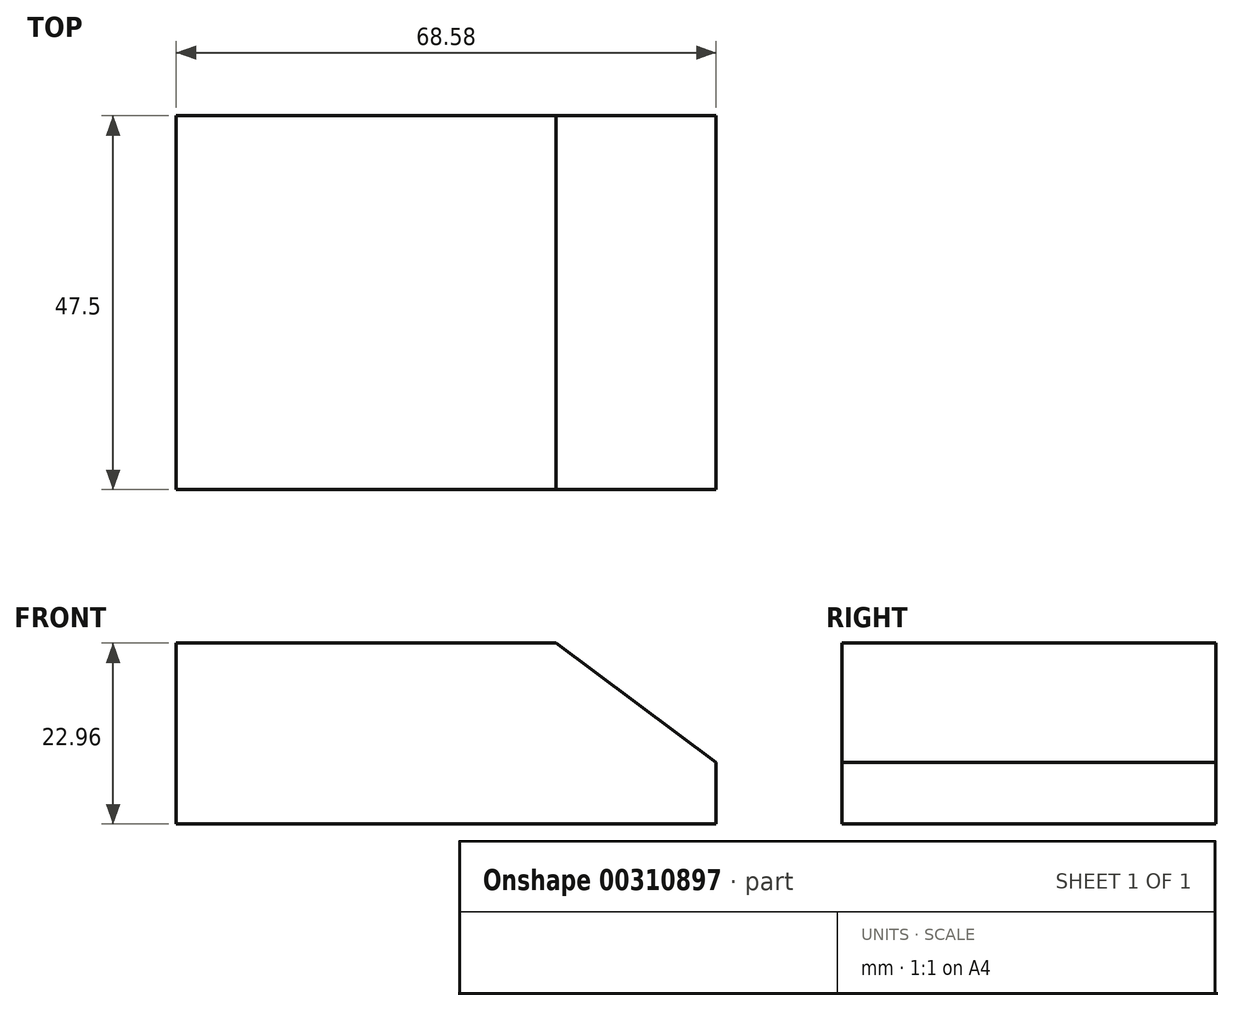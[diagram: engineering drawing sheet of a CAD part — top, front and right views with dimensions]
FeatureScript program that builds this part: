
annotation { "Feature Type Name" : "Feature", "Feature Type Description" : "" }
export const myFeature = defineFeature(function(context is Context, id is Id, definition is map)
    precondition{}
    {
        {
            var Q0;
            Q0=qCreatedBy(makeId("Front.planeOp"),FACE);
            var sketch = newSketch(context, id + "F0", { "sketchPlane" : qUnion([Q0])});
            skLineSegment(sketch, "E0", {"start": v(-39.86, -43.36) * mm, "end": v(28.72, -43.36) * mm});
            skLineSegment(sketch, "E1", {"start": v(28.72, -43.36) * mm, "end": v(28.72, -35.54) * mm});
            skLineSegment(sketch, "E2", {"start": v(28.72, -35.54) * mm, "end": v(8.35, -20.4) * mm});
            skLineSegment(sketch, "E3", {"start": v(8.35, -20.4) * mm, "end": v(-39.86, -20.4) * mm});
            skLineSegment(sketch, "E4", {"start": v(-39.86, -20.4) * mm, "end": v(-39.86, -43.36) * mm});
            skSolve(sketch);
        }
        {
            var Q0;
            Q0=makeQuery(id+"F0.imprint","IMPRINT",FACE,{"disambiguationData":[TD([[makeQuery(id+"F0.imprint","IMPRINT",EDGE,{"derivedFrom":sQuery(id+"F0.wireOp",EDGE,"E0")}),1.0]])]});
            extrude(context, id + "F1", {"entities" : qUnion([Q0]), "depth" : 47.5 * mm});
        }
    });
